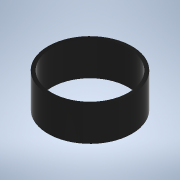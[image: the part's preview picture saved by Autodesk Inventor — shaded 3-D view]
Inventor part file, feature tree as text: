
AUTODESK INVENTOR PART (.ipt)
format: ipt  version: 2022 (Build 260153000, 153)  size: 98,304 bytes
history: native  units: in
note: dims shown in document units (in); Inventor stores cm internally (conversion verified against a paired STEP export)
features: extrude x1, sketch x1
ambient origin geometry x8: Origin, YZ Plane, XZ Plane, XY Plane, X Axis, Y Axis, Z Axis, Center Point
bodies: Solid1 (feature_tree)
feature tree (2):
  extrude  "Extrusion1"  Depth=0.6791in
  sketch  "Sketch1"  dims[d0=1.6732in d1=0.0689in d2=0.6791in d3=0.0in]
